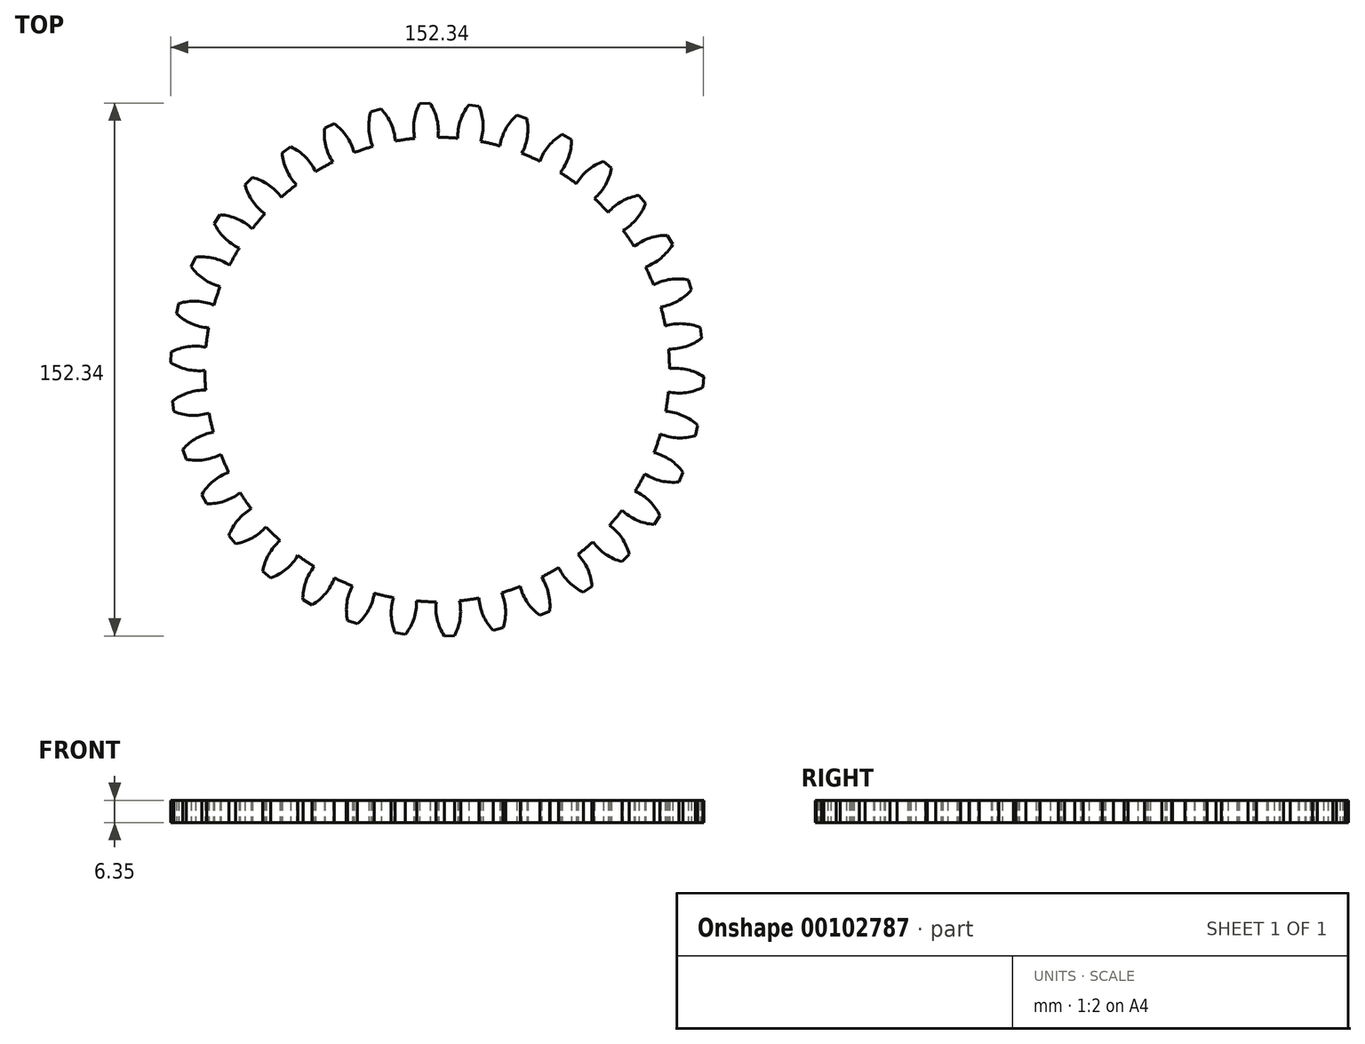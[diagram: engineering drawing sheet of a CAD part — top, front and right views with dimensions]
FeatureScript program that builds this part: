
annotation { "Feature Type Name" : "Feature", "Feature Type Description" : "" }
export const myFeature = defineFeature(function(context is Context, id is Id, definition is map)
    precondition{}
    {
        {
            var Q0;
            Q0=qCreatedBy(makeId("Top.planeOp"),FACE);
            var sketch = newSketch(context, id + "F0", { "sketchPlane" : qUnion([Q0])});
            skCircle(sketch, "E0", {"center": v(0, 0) * mm, "radius": 76.2 * mm, "construction": true});
            skCircle(sketch, "E1", {"center": v(0, 0) * mm, "radius": 71.37 * mm, "construction": true});
            skCircle(sketch, "E2", {"center": v(0, 0) * mm, "radius": 66.42 * mm});
            skLineSegment(sketch, "E3", {"start": v(0, 0) * mm, "end": v(0, 120.55) * mm, "construction": true});
            skLineSegment(sketch, "E4", {"start": v(0, 0) * mm, "end": v(-5.66, 122.47) * mm, "construction": true});
            skLineSegment(sketch, "E5", {"start": v(0, 71.37) * mm, "end": v(-69.1, 80.27) * mm, "construction": true});
            skLineSegment(sketch, "E6", {"start": v(0, 71.37) * mm, "end": v(-41.61, 62.02) * mm, "construction": true});
            skCircle(sketch, "E7", {"center": v(0, 71.37) * mm, "radius": 14.67 * mm, "construction": true});
            skArc(sketch, "E8", {"start": v(-3.62, 78.2) * mm, "mid": v(-23.1, 79.9) * mm, "end": v(-26.95, 60.7) * mm, "construction": true});
            skArc(sketch, "E9", {"start": v(-26.95, 60.7) * mm, "mid": v(-11.3, 53.8) * mm, "end": v(0.25, 66.42) * mm, "construction": true});
            skArc(sketch, "E10", {"start": v(-2.03, 76.17) * mm, "mid": v(-2.78, 77.22) * mm, "end": v(-3.62, 78.2) * mm, "construction": true});
            skArc(sketch, "E11", {"start": v(0.25, 66.42) * mm, "mid": v(-0.03, 71.5) * mm, "end": v(-2.03, 76.17) * mm});
            skArc(sketch, "E12.MirrorCS", {"start": v(-6.38, 66.11) * mm, "mid": v(-6.57, 71.2) * mm, "end": v(-5.01, 76.04) * mm});
            skLineSegment(sketch, "E13.1.0", {"start": v(0, 0) * mm, "end": v(-28.07, 119.34) * mm, "construction": true});
            skArc(sketch, "E13.1.1", {"start": v(-11.96, 65.34) * mm, "mid": v(-13.17, 70.27) * mm, "end": v(-15.99, 74.5) * mm});
            skArc(sketch, "E13.1.2", {"start": v(-18.42, 63.82) * mm, "mid": v(-19.54, 68.78) * mm, "end": v(-18.9, 73.82) * mm});
            skLineSegment(sketch, "E13.2.0", {"start": v(0, 0) * mm, "end": v(-49.52, 112.15) * mm, "construction": true});
            skArc(sketch, "E13.2.1", {"start": v(-23.76, 62.03) * mm, "mid": v(-25.85, 66.66) * mm, "end": v(-29.4, 70.3) * mm});
            skArc(sketch, "E13.2.2", {"start": v(-29.83, 59.34) * mm, "mid": v(-31.84, 64.01) * mm, "end": v(-32.14, 69.1) * mm});
            skLineSegment(sketch, "E13.3.0", {"start": v(0, 0) * mm, "end": v(-69.29, 101.15) * mm, "construction": true});
            skArc(sketch, "E13.3.1", {"start": v(-34.75, 56.6) * mm, "mid": v(-37.66, 60.77) * mm, "end": v(-41.82, 63.7) * mm});
            skArc(sketch, "E13.3.2", {"start": v(-40.23, 52.85) * mm, "mid": v(-43.06, 57.07) * mm, "end": v(-44.29, 62) * mm});
            skLineSegment(sketch, "E13.4.0", {"start": v(0, 0) * mm, "end": v(-86.7, 86.7) * mm, "construction": true});
            skArc(sketch, "E13.4.1", {"start": v(-44.56, 49.26) * mm, "mid": v(-48.19, 52.82) * mm, "end": v(-52.82, 54.93) * mm});
            skArc(sketch, "E13.4.2", {"start": v(-49.26, 44.56) * mm, "mid": v(-52.82, 48.19) * mm, "end": v(-54.93, 52.82) * mm});
            skLineSegment(sketch, "E13.5.0", {"start": v(0, 0) * mm, "end": v(-101.15, 69.29) * mm, "construction": true});
            skArc(sketch, "E13.5.1", {"start": v(-52.85, 40.23) * mm, "mid": v(-57.07, 43.06) * mm, "end": v(-62, 44.29) * mm});
            skArc(sketch, "E13.5.2", {"start": v(-56.6, 34.75) * mm, "mid": v(-60.77, 37.66) * mm, "end": v(-63.7, 41.82) * mm});
            skLineSegment(sketch, "E13.6.0", {"start": v(0, 0) * mm, "end": v(-112.15, 49.52) * mm, "construction": true});
            skArc(sketch, "E13.6.1", {"start": v(-59.34, 29.83) * mm, "mid": v(-64.01, 31.84) * mm, "end": v(-69.1, 32.14) * mm});
            skArc(sketch, "E13.6.2", {"start": v(-62.03, 23.76) * mm, "mid": v(-66.66, 25.85) * mm, "end": v(-70.3, 29.4) * mm});
            skLineSegment(sketch, "E13.7.0", {"start": v(0, 0) * mm, "end": v(-119.34, 28.07) * mm, "construction": true});
            skArc(sketch, "E13.7.1", {"start": v(-63.82, 18.42) * mm, "mid": v(-68.78, 19.54) * mm, "end": v(-73.82, 18.9) * mm});
            skArc(sketch, "E13.7.2", {"start": v(-65.34, 11.96) * mm, "mid": v(-70.27, 13.17) * mm, "end": v(-74.5, 15.99) * mm});
            skLineSegment(sketch, "E13.8.0", {"start": v(0, 0) * mm, "end": v(-122.47, 5.66) * mm, "construction": true});
            skArc(sketch, "E13.8.1", {"start": v(-66.11, 6.38) * mm, "mid": v(-71.2, 6.57) * mm, "end": v(-76.04, 5.01) * mm});
            skArc(sketch, "E13.8.2", {"start": v(-66.42, -0.25) * mm, "mid": v(-71.5, 0.03) * mm, "end": v(-76.17, 2.03) * mm});
            skLineSegment(sketch, "E13.9.0", {"start": v(0, 0) * mm, "end": v(-121.43, -16.94) * mm, "construction": true});
            skArc(sketch, "E13.9.1", {"start": v(-66.16, -5.88) * mm, "mid": v(-71.19, -6.63) * mm, "end": v(-75.66, -9.05) * mm});
            skArc(sketch, "E13.9.2", {"start": v(-65.24, -12.45) * mm, "mid": v(-70.29, -13.1) * mm, "end": v(-75.25, -12) * mm});
            skLineSegment(sketch, "E13.10.0", {"start": v(0, 0) * mm, "end": v(-116.25, -38.96) * mm, "construction": true});
            skArc(sketch, "E13.10.1", {"start": v(-63.95, -17.93) * mm, "mid": v(-68.76, -19.6) * mm, "end": v(-72.71, -22.8) * mm});
            skArc(sketch, "E13.10.2", {"start": v(-61.84, -24.23) * mm, "mid": v(-66.68, -25.8) * mm, "end": v(-71.76, -25.63) * mm});
            skLineSegment(sketch, "E13.11.0", {"start": v(0, 0) * mm, "end": v(-107.1, -59.66) * mm, "construction": true});
            skArc(sketch, "E13.11.1", {"start": v(-59.57, -29.38) * mm, "mid": v(-63.99, -31.9) * mm, "end": v(-67.28, -35.77) * mm});
            skArc(sketch, "E13.11.2", {"start": v(-56.34, -35.18) * mm, "mid": v(-60.8, -37.61) * mm, "end": v(-65.83, -38.38) * mm});
            skLineSegment(sketch, "E13.12.0", {"start": v(0, 0) * mm, "end": v(-94.32, -78.32) * mm, "construction": true});
            skArc(sketch, "E13.12.1", {"start": v(-53.16, -39.82) * mm, "mid": v(-57.04, -43.1) * mm, "end": v(-59.57, -47.52) * mm});
            skArc(sketch, "E13.12.2", {"start": v(-48.91, -44.93) * mm, "mid": v(-52.86, -48.15) * mm, "end": v(-57.66, -49.82) * mm});
            skLineSegment(sketch, "E13.13.0", {"start": v(0, 0) * mm, "end": v(-78.32, -94.32) * mm, "construction": true});
            skArc(sketch, "E13.13.1", {"start": v(-44.93, -48.91) * mm, "mid": v(-48.15, -52.86) * mm, "end": v(-49.82, -57.66) * mm});
            skArc(sketch, "E13.13.2", {"start": v(-39.82, -53.16) * mm, "mid": v(-43.1, -57.04) * mm, "end": v(-47.52, -59.57) * mm});
            skLineSegment(sketch, "E13.14.0", {"start": v(0, 0) * mm, "end": v(-59.66, -107.1) * mm, "construction": true});
            skArc(sketch, "E13.14.1", {"start": v(-35.18, -56.34) * mm, "mid": v(-37.61, -60.8) * mm, "end": v(-38.38, -65.83) * mm});
            skArc(sketch, "E13.14.2", {"start": v(-29.38, -59.57) * mm, "mid": v(-31.9, -63.99) * mm, "end": v(-35.77, -67.28) * mm});
            skLineSegment(sketch, "E13.15.0", {"start": v(0, 0) * mm, "end": v(-38.96, -116.25) * mm, "construction": true});
            skArc(sketch, "E13.15.1", {"start": v(-24.23, -61.84) * mm, "mid": v(-25.8, -66.68) * mm, "end": v(-25.63, -71.76) * mm});
            skArc(sketch, "E13.15.2", {"start": v(-17.93, -63.95) * mm, "mid": v(-19.6, -68.76) * mm, "end": v(-22.8, -72.71) * mm});
            skLineSegment(sketch, "E13.16.0", {"start": v(0, 0) * mm, "end": v(-16.94, -121.43) * mm, "construction": true});
            skArc(sketch, "E13.16.1", {"start": v(-12.45, -65.24) * mm, "mid": v(-13.1, -70.29) * mm, "end": v(-12, -75.25) * mm});
            skArc(sketch, "E13.16.2", {"start": v(-5.88, -66.16) * mm, "mid": v(-6.63, -71.19) * mm, "end": v(-9.05, -75.66) * mm});
            skLineSegment(sketch, "E13.17.0", {"start": v(0, 0) * mm, "end": v(5.66, -122.47) * mm, "construction": true});
            skArc(sketch, "E13.17.1", {"start": v(-0.25, -66.42) * mm, "mid": v(0.03, -71.5) * mm, "end": v(2.03, -76.17) * mm});
            skArc(sketch, "E13.17.2", {"start": v(6.38, -66.11) * mm, "mid": v(6.57, -71.2) * mm, "end": v(5.01, -76.04) * mm});
            skLineSegment(sketch, "E13.18.0", {"start": v(0, 0) * mm, "end": v(28.07, -119.34) * mm, "construction": true});
            skArc(sketch, "E13.18.1", {"start": v(11.96, -65.34) * mm, "mid": v(13.17, -70.27) * mm, "end": v(15.99, -74.5) * mm});
            skArc(sketch, "E13.18.2", {"start": v(18.42, -63.82) * mm, "mid": v(19.54, -68.78) * mm, "end": v(18.9, -73.82) * mm});
            skLineSegment(sketch, "E13.19.0", {"start": v(0, 0) * mm, "end": v(49.52, -112.15) * mm, "construction": true});
            skArc(sketch, "E13.19.1", {"start": v(23.76, -62.03) * mm, "mid": v(25.85, -66.66) * mm, "end": v(29.4, -70.3) * mm});
            skArc(sketch, "E13.19.2", {"start": v(29.83, -59.34) * mm, "mid": v(31.84, -64.01) * mm, "end": v(32.14, -69.1) * mm});
            skLineSegment(sketch, "E13.20.0", {"start": v(0, 0) * mm, "end": v(69.29, -101.15) * mm, "construction": true});
            skArc(sketch, "E13.20.1", {"start": v(34.75, -56.6) * mm, "mid": v(37.66, -60.77) * mm, "end": v(41.82, -63.7) * mm});
            skArc(sketch, "E13.20.2", {"start": v(40.23, -52.85) * mm, "mid": v(43.06, -57.07) * mm, "end": v(44.29, -62) * mm});
            skLineSegment(sketch, "E13.21.0", {"start": v(0, 0) * mm, "end": v(86.7, -86.7) * mm, "construction": true});
            skArc(sketch, "E13.21.1", {"start": v(44.56, -49.26) * mm, "mid": v(48.19, -52.82) * mm, "end": v(52.82, -54.93) * mm});
            skArc(sketch, "E13.21.2", {"start": v(49.26, -44.56) * mm, "mid": v(52.82, -48.19) * mm, "end": v(54.93, -52.82) * mm});
            skLineSegment(sketch, "E13.22.0", {"start": v(0, 0) * mm, "end": v(101.15, -69.29) * mm, "construction": true});
            skArc(sketch, "E13.22.1", {"start": v(52.85, -40.23) * mm, "mid": v(57.07, -43.06) * mm, "end": v(62, -44.29) * mm});
            skArc(sketch, "E13.22.2", {"start": v(56.6, -34.75) * mm, "mid": v(60.77, -37.66) * mm, "end": v(63.7, -41.82) * mm});
            skLineSegment(sketch, "E13.23.0", {"start": v(0, 0) * mm, "end": v(112.15, -49.52) * mm, "construction": true});
            skArc(sketch, "E13.23.1", {"start": v(59.34, -29.83) * mm, "mid": v(64.01, -31.84) * mm, "end": v(69.1, -32.14) * mm});
            skArc(sketch, "E13.23.2", {"start": v(62.03, -23.76) * mm, "mid": v(66.66, -25.85) * mm, "end": v(70.3, -29.4) * mm});
            skLineSegment(sketch, "E13.24.0", {"start": v(0, 0) * mm, "end": v(119.34, -28.07) * mm, "construction": true});
            skArc(sketch, "E13.24.1", {"start": v(63.82, -18.42) * mm, "mid": v(68.78, -19.54) * mm, "end": v(73.82, -18.9) * mm});
            skArc(sketch, "E13.24.2", {"start": v(65.34, -11.96) * mm, "mid": v(70.27, -13.17) * mm, "end": v(74.5, -15.99) * mm});
            skLineSegment(sketch, "E13.25.0", {"start": v(0, 0) * mm, "end": v(122.47, -5.66) * mm, "construction": true});
            skArc(sketch, "E13.25.1", {"start": v(66.11, -6.38) * mm, "mid": v(71.2, -6.57) * mm, "end": v(76.04, -5.01) * mm});
            skArc(sketch, "E13.25.2", {"start": v(66.42, 0.25) * mm, "mid": v(71.5, -0.03) * mm, "end": v(76.17, -2.03) * mm});
            skLineSegment(sketch, "E13.26.0", {"start": v(0, 0) * mm, "end": v(121.43, 16.94) * mm, "construction": true});
            skArc(sketch, "E13.26.1", {"start": v(66.16, 5.88) * mm, "mid": v(71.19, 6.63) * mm, "end": v(75.66, 9.05) * mm});
            skArc(sketch, "E13.26.2", {"start": v(65.24, 12.45) * mm, "mid": v(70.29, 13.1) * mm, "end": v(75.25, 12) * mm});
            skLineSegment(sketch, "E13.27.0", {"start": v(0, 0) * mm, "end": v(116.25, 38.96) * mm, "construction": true});
            skArc(sketch, "E13.27.1", {"start": v(63.95, 17.93) * mm, "mid": v(68.76, 19.6) * mm, "end": v(72.71, 22.8) * mm});
            skArc(sketch, "E13.27.2", {"start": v(61.84, 24.23) * mm, "mid": v(66.68, 25.8) * mm, "end": v(71.76, 25.63) * mm});
            skLineSegment(sketch, "E13.28.0", {"start": v(0, 0) * mm, "end": v(107.1, 59.66) * mm, "construction": true});
            skArc(sketch, "E13.28.1", {"start": v(59.57, 29.38) * mm, "mid": v(63.99, 31.9) * mm, "end": v(67.28, 35.77) * mm});
            skArc(sketch, "E13.28.2", {"start": v(56.34, 35.18) * mm, "mid": v(60.8, 37.61) * mm, "end": v(65.83, 38.38) * mm});
            skLineSegment(sketch, "E13.29.0", {"start": v(0, 0) * mm, "end": v(94.32, 78.32) * mm, "construction": true});
            skArc(sketch, "E13.29.1", {"start": v(53.16, 39.82) * mm, "mid": v(57.04, 43.1) * mm, "end": v(59.57, 47.52) * mm});
            skArc(sketch, "E13.29.2", {"start": v(48.91, 44.93) * mm, "mid": v(52.86, 48.15) * mm, "end": v(57.66, 49.82) * mm});
            skLineSegment(sketch, "E13.30.0", {"start": v(0, 0) * mm, "end": v(78.32, 94.32) * mm, "construction": true});
            skArc(sketch, "E13.30.1", {"start": v(44.93, 48.91) * mm, "mid": v(48.15, 52.86) * mm, "end": v(49.82, 57.66) * mm});
            skArc(sketch, "E13.30.2", {"start": v(39.82, 53.16) * mm, "mid": v(43.1, 57.04) * mm, "end": v(47.52, 59.57) * mm});
            skLineSegment(sketch, "E13.31.0", {"start": v(0, 0) * mm, "end": v(59.66, 107.1) * mm, "construction": true});
            skArc(sketch, "E13.31.1", {"start": v(35.18, 56.34) * mm, "mid": v(37.61, 60.8) * mm, "end": v(38.38, 65.83) * mm});
            skArc(sketch, "E13.31.2", {"start": v(29.38, 59.57) * mm, "mid": v(31.9, 63.99) * mm, "end": v(35.77, 67.28) * mm});
            skLineSegment(sketch, "E13.32.0", {"start": v(0, 0) * mm, "end": v(38.96, 116.25) * mm, "construction": true});
            skArc(sketch, "E13.32.1", {"start": v(24.23, 61.84) * mm, "mid": v(25.8, 66.68) * mm, "end": v(25.63, 71.76) * mm});
            skArc(sketch, "E13.32.2", {"start": v(17.93, 63.95) * mm, "mid": v(19.6, 68.76) * mm, "end": v(22.8, 72.71) * mm});
            skLineSegment(sketch, "E13.33.0", {"start": v(0, 0) * mm, "end": v(16.94, 121.43) * mm, "construction": true});
            skArc(sketch, "E13.33.1", {"start": v(12.45, 65.24) * mm, "mid": v(13.1, 70.29) * mm, "end": v(12, 75.25) * mm});
            skArc(sketch, "E13.33.2", {"start": v(5.88, 66.16) * mm, "mid": v(6.63, 71.19) * mm, "end": v(9.05, 75.66) * mm});
            skPoint(sketch, "E14", {"position": v(-30.78, 69.7) * mm});
            skPoint(sketch, "E15", {"position": v(-17.45, 74.18) * mm});
            skLineSegment(sketch, "E16", {"start": v(-5.01, 76.04) * mm, "end": v(-2.03, 76.17) * mm});
            skLineSegment(sketch, "E17.1.0", {"start": v(-18.9, 73.82) * mm, "end": v(-15.99, 74.5) * mm});
            skLineSegment(sketch, "E17.2.0", {"start": v(-32.14, 69.1) * mm, "end": v(-29.4, 70.3) * mm});
            skLineSegment(sketch, "E17.3.0", {"start": v(-44.29, 62) * mm, "end": v(-41.82, 63.7) * mm});
            skLineSegment(sketch, "E17.4.0", {"start": v(-54.93, 52.82) * mm, "end": v(-52.82, 54.93) * mm});
            skLineSegment(sketch, "E17.5.0", {"start": v(-63.7, 41.82) * mm, "end": v(-62, 44.29) * mm});
            skLineSegment(sketch, "E17.6.0", {"start": v(-70.3, 29.4) * mm, "end": v(-69.1, 32.14) * mm});
            skLineSegment(sketch, "E17.7.0", {"start": v(-74.5, 15.99) * mm, "end": v(-73.82, 18.9) * mm});
            skLineSegment(sketch, "E17.8.0", {"start": v(-76.17, 2.03) * mm, "end": v(-76.04, 5.01) * mm});
            skLineSegment(sketch, "E17.9.0", {"start": v(-75.25, -12) * mm, "end": v(-75.66, -9.05) * mm});
            skLineSegment(sketch, "E17.10.0", {"start": v(-71.76, -25.63) * mm, "end": v(-72.71, -22.8) * mm});
            skLineSegment(sketch, "E17.11.0", {"start": v(-65.83, -38.38) * mm, "end": v(-67.28, -35.77) * mm});
            skLineSegment(sketch, "E17.12.0", {"start": v(-57.66, -49.82) * mm, "end": v(-59.57, -47.52) * mm});
            skLineSegment(sketch, "E17.13.0", {"start": v(-47.52, -59.57) * mm, "end": v(-49.82, -57.66) * mm});
            skLineSegment(sketch, "E17.14.0", {"start": v(-35.77, -67.28) * mm, "end": v(-38.38, -65.83) * mm});
            skLineSegment(sketch, "E17.15.0", {"start": v(-22.8, -72.71) * mm, "end": v(-25.63, -71.76) * mm});
            skLineSegment(sketch, "E17.16.0", {"start": v(-9.05, -75.66) * mm, "end": v(-12, -75.25) * mm});
            skLineSegment(sketch, "E17.17.0", {"start": v(5.01, -76.04) * mm, "end": v(2.03, -76.17) * mm});
            skLineSegment(sketch, "E17.18.0", {"start": v(18.9, -73.82) * mm, "end": v(15.99, -74.5) * mm});
            skLineSegment(sketch, "E17.19.0", {"start": v(32.14, -69.1) * mm, "end": v(29.4, -70.3) * mm});
            skLineSegment(sketch, "E17.20.0", {"start": v(44.29, -62) * mm, "end": v(41.82, -63.7) * mm});
            skLineSegment(sketch, "E17.21.0", {"start": v(54.93, -52.82) * mm, "end": v(52.82, -54.93) * mm});
            skLineSegment(sketch, "E17.22.0", {"start": v(63.7, -41.82) * mm, "end": v(62, -44.29) * mm});
            skLineSegment(sketch, "E17.23.0", {"start": v(70.3, -29.4) * mm, "end": v(69.1, -32.14) * mm});
            skLineSegment(sketch, "E17.24.0", {"start": v(74.5, -15.99) * mm, "end": v(73.82, -18.9) * mm});
            skLineSegment(sketch, "E17.25.0", {"start": v(76.17, -2.03) * mm, "end": v(76.04, -5.01) * mm});
            skLineSegment(sketch, "E17.26.0", {"start": v(75.25, 12) * mm, "end": v(75.66, 9.05) * mm});
            skLineSegment(sketch, "E17.27.0", {"start": v(71.76, 25.63) * mm, "end": v(72.71, 22.8) * mm});
            skLineSegment(sketch, "E17.28.0", {"start": v(65.83, 38.38) * mm, "end": v(67.28, 35.77) * mm});
            skLineSegment(sketch, "E17.29.0", {"start": v(57.66, 49.82) * mm, "end": v(59.57, 47.52) * mm});
            skLineSegment(sketch, "E17.30.0", {"start": v(47.52, 59.57) * mm, "end": v(49.82, 57.66) * mm});
            skLineSegment(sketch, "E17.31.0", {"start": v(35.77, 67.28) * mm, "end": v(38.38, 65.83) * mm});
            skLineSegment(sketch, "E17.32.0", {"start": v(22.8, 72.71) * mm, "end": v(25.63, 71.76) * mm});
            skLineSegment(sketch, "E17.33.0", {"start": v(9.05, 75.66) * mm, "end": v(12, 75.25) * mm});
            skSolve(sketch);
        }
        {
            var Q0;
            Q0 = qSketchRegion(id + "F0", true);
            extrude(context, id + "F1", {"entities" : qUnion([Q0]), "depth" : 6.35 * mm});
        }
    });
